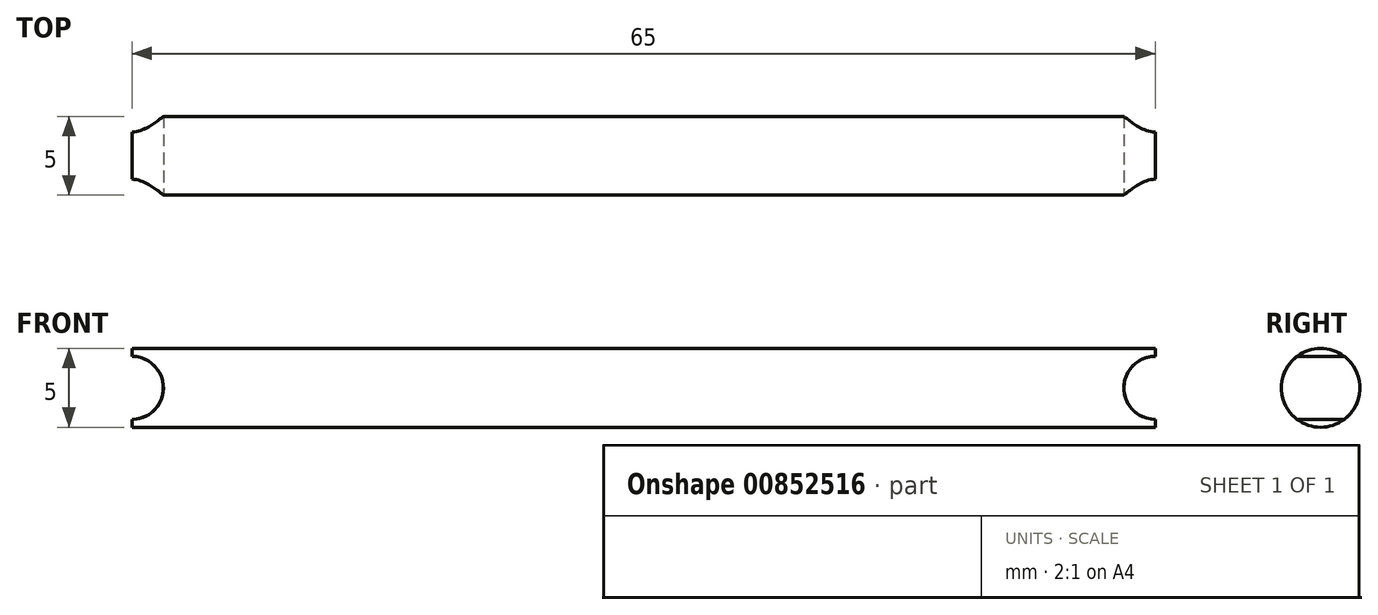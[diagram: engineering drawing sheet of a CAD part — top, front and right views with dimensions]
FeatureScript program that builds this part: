
annotation { "Feature Type Name" : "Feature", "Feature Type Description" : "" }
export const myFeature = defineFeature(function(context is Context, id is Id, definition is map)
    precondition{}
    {
        {
            assignVariable(context, id + "F0", {"name" : "RodLength", "anyValue" : 65});
        }
        {
            var Q0;
            Q0=qCreatedBy(makeId("Right.planeOp"),FACE);
            var sketch = newSketch(context, id + "F1", { "sketchPlane" : qUnion([Q0])});
            skCircle(sketch, "E0", {"center": v(0, 0) * mm, "radius": 2.5 * mm});
            skSolve(sketch);
        }
        {
            var Q0;
            Q0 = qSketchRegion(id + "F1", true);
            extrude(context, id + "F2", {"entities" : qUnion([Q0]), "endBound" : BoundingType.SYMMETRIC, "depth" : (getVariable(context, 'RodLength')) * mm, "offsetDistance" : 25 * mm});
        }
        {
            var Q0;
            Q0=qCreatedBy(makeId("Front.planeOp"),FACE);
            var sketch = newSketch(context, id + "F3", { "sketchPlane" : qUnion([Q0])});
            skLineSegment(sketch, "E1.0", {"start": v(-32.5, 2.5) * mm, "end": v(-32.5, -2.5) * mm, "construction": true});
            skPoint(sketch, "E2", {"position": v(-32.5, 0) * mm});
            skCircle(sketch, "E3", {"center": v(-32.5, 0) * mm, "radius": 2 * mm});
            skCircle(sketch, "E4.MirrorC", {"center": v(32.5, 0) * mm, "radius": 2 * mm});
            skSolve(sketch);
        }
        {
            var Q0;
            Q0 = qSketchRegion(id + "F3", true);
            extrude(context, id + "F4", {"entities" : qUnion([Q0]), "operationType" : NewBodyOperationType.REMOVE, "endBound" : BoundingType.THROUGH_ALL, "oppositeDirection" : true, "depth" : 25 * mm, "offsetDistance" : 25 * mm, "hasSecondDirection" : true, "secondDirectionBound" : SecondDirectionBoundingType.THROUGH_ALL, "secondDirectionOppositeDirection" : false, "secondDirectionDepth" : 25 * mm});
        }
    });
